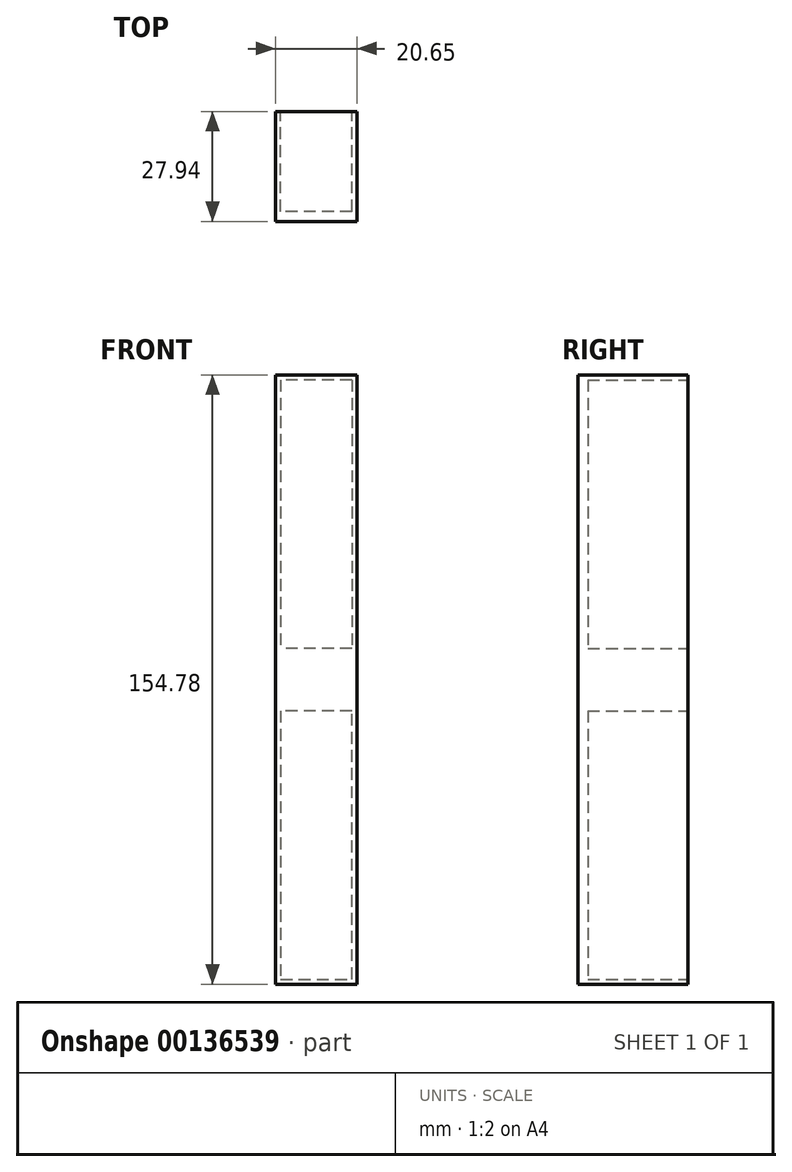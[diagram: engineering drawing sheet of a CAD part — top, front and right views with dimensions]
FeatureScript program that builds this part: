
annotation { "Feature Type Name" : "Feature", "Feature Type Description" : "" }
export const myFeature = defineFeature(function(context is Context, id is Id, definition is map)
    precondition{}
    {
        {
            var Q0;
            Q0=qCreatedBy(makeId("Front.planeOp"),FACE);
            var sketch = newSketch(context, id + "F0", { "sketchPlane" : qUnion([Q0])});
            skLineSegment(sketch, "E0.bottom", {"start": v(0, 0) * mm, "end": v(20.64, 0) * mm});
            skLineSegment(sketch, "E0.top", {"start": v(0, 72.61) * mm, "end": v(20.64, 72.61) * mm});
            skLineSegment(sketch, "E0.left", {"start": v(0, 0) * mm, "end": v(0, 72.61) * mm});
            skLineSegment(sketch, "E0.right", {"start": v(20.64, 0) * mm, "end": v(20.64, 72.61) * mm});
            skPoint(sketch, "E1.end.orphan", {"position": v(15.1, 0) * mm});
            skLineSegment(sketch, "E2.bottom", {"start": v(20.65, 154.78) * mm, "end": v(0, 154.78) * mm});
            skLineSegment(sketch, "E2.top", {"start": v(20.65, 82.14) * mm, "end": v(0, 82.14) * mm});
            skLineSegment(sketch, "E2.left", {"start": v(20.65, 154.78) * mm, "end": v(20.65, 82.14) * mm});
            skLineSegment(sketch, "E2.right", {"start": v(0, 154.78) * mm, "end": v(0, 82.14) * mm});
            skLineSegment(sketch, "E3", {"start": v(20.65, 82.14) * mm, "end": v(20.64, 72.61) * mm});
            skLineSegment(sketch, "E4", {"start": v(0, 82.14) * mm, "end": v(0, 72.61) * mm});
            skSolve(sketch);
        }
        {
            var Q0;
            Q0=makeQuery(id+"F0.imprint","IMPRINT",FACE,{"disambiguationData":[TD([[makeQuery(id+"F0.imprint","IMPRINT",EDGE,{"derivedFrom":sQuery(id+"F0.wireOp",EDGE,"E2.bottom")}),1.0]])]});
            var Q1;
            Q1=makeQuery(id+"F0.imprint","IMPRINT",FACE,{"disambiguationData":[TD([[makeQuery(id+"F0.imprint","IMPRINT",EDGE,{"derivedFrom":sQuery(id+"F0.wireOp",EDGE,"E0.top")}),1.0]])]});
            var Q2;
            Q2=makeQuery(id+"F0.imprint","IMPRINT",FACE,{"disambiguationData":[TD([[makeQuery(id+"F0.imprint","IMPRINT",EDGE,{"derivedFrom":sQuery(id+"F0.wireOp",EDGE,"E0.bottom")}),1.0]])]});
            extrude(context, id + "F1", {"entities" : qUnion([Q0, Q1, Q2]), "depth" : 27.94 * mm});
        }
        {
            var Q0;
            Q0=makeQuery(id+"F1.opExtrude","CAP_FACE",FACE,{"disambiguationData":[OSD([sQuery(id+"F0.wireOp",EDGE,"E0.bottom"),sQuery(id+"F0.wireOp",EDGE,"E0.left"),sQuery(id+"F0.wireOp",EDGE,"E0.right"),sQuery(id+"F0.wireOp",EDGE,"E2.bottom"),sQuery(id+"F0.wireOp",EDGE,"E2.left"),sQuery(id+"F0.wireOp",EDGE,"E2.right"),sQuery(id+"F0.wireOp",EDGE,"E3"),sQuery(id+"F0.wireOp",EDGE,"E4")])],"isStart":true});
            var sketch = newSketch(context, id + "F2", { "sketchPlane" : qUnion([Q0])});
            skLineSegment(sketch, "E5.0", {"start": v(-19.38, 153.51) * mm, "end": v(-19.38, 82.14) * mm});
            skLineSegment(sketch, "E5.1", {"start": v(-1.27, 153.51) * mm, "end": v(-1.27, 1.27) * mm});
            skLineSegment(sketch, "E5.2", {"start": v(-1.27, 1.27) * mm, "end": v(-19.37, 1.27) * mm});
            skLineSegment(sketch, "E5.3", {"start": v(-19.38, 153.51) * mm, "end": v(-1.27, 153.51) * mm});
            skLineSegment(sketch, "E5.4", {"start": v(-19.37, 1.27) * mm, "end": v(-19.37, 72.61) * mm});
            skLineSegment(sketch, "E5.5", {"start": v(-19.38, 82.14) * mm, "end": v(-19.37, 72.61) * mm});
            skLineSegment(sketch, "E6", {"start": v(-19.37, 69.44) * mm, "end": v(-1.27, 69.44) * mm});
            skLineSegment(sketch, "E7", {"start": v(-19.38, 85.31) * mm, "end": v(-1.27, 85.31) * mm});
            skSolve(sketch);
        }
        {
            var Q0;
            {var subQ0=sQuery(id+"F2.wireOp",EDGE,"E5.2");Q0=makeQuery(id+"F2.imprint","IMPRINT",FACE,{"disambiguationData":[TD([[makeQuery(id+"F2.imprint","IMPRINT",EDGE,{"derivedFrom":subQ0}),-1.0]])]});}
            var Q1;
            {var subQ0=sQuery(id+"F2.wireOp",EDGE,"E5.3");Q1=makeQuery(id+"F2.imprint","IMPRINT",FACE,{"disambiguationData":[TD([[makeQuery(id+"F2.imprint","IMPRINT",EDGE,{"derivedFrom":subQ0}),-1.0]])]});}
            extrude(context, id + "F3", {"entities" : qUnion([Q0, Q1]), "operationType" : NewBodyOperationType.REMOVE, "oppositeDirection" : true, "depth" : 25.4 * mm});
        }
    });
